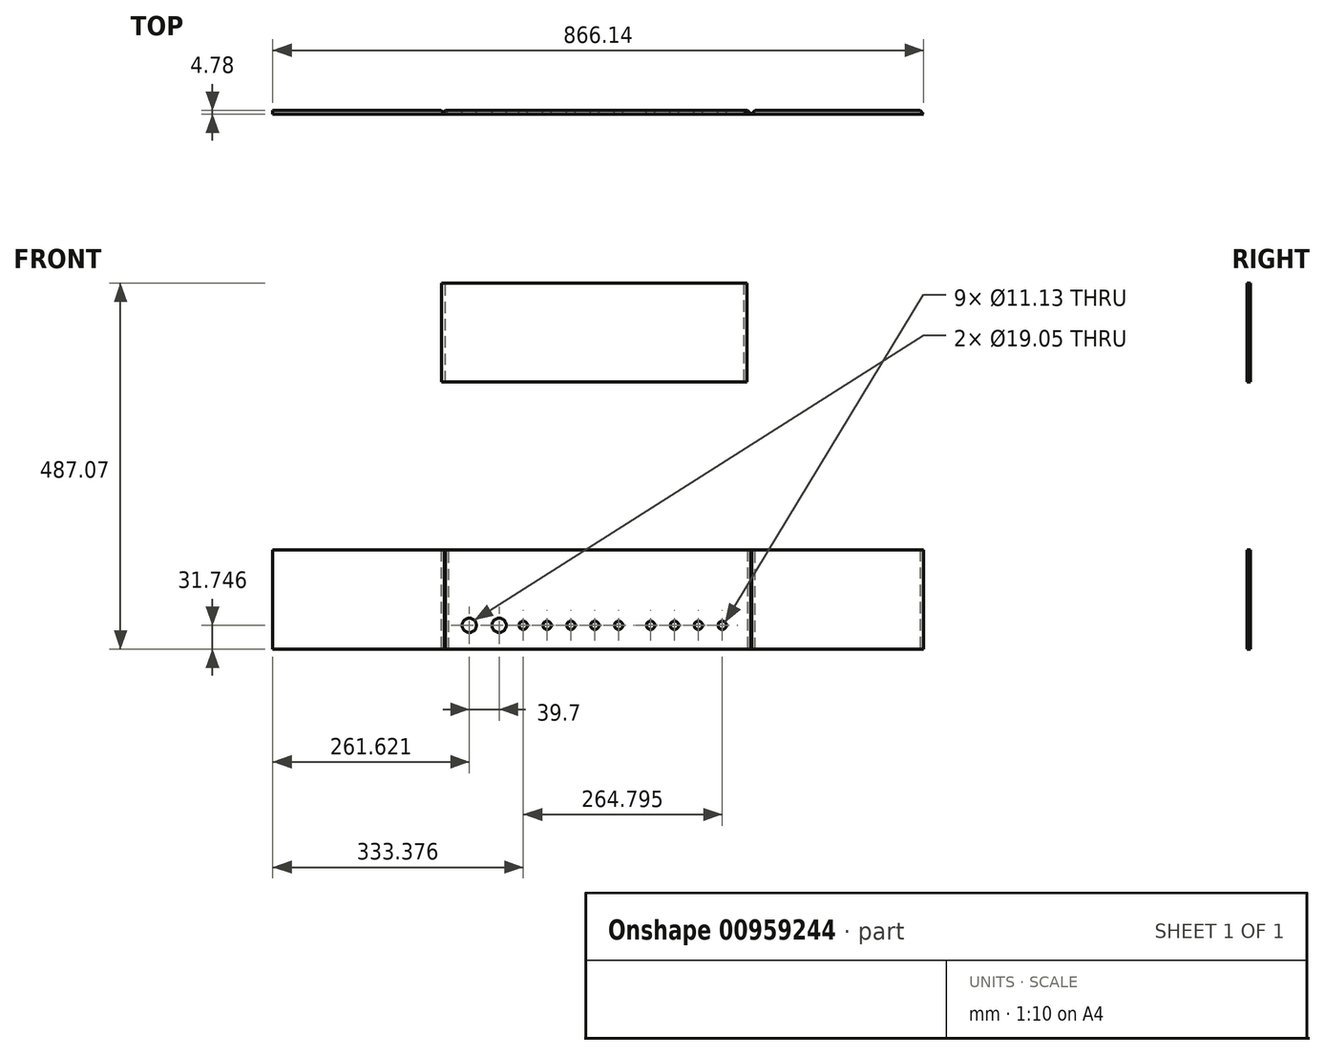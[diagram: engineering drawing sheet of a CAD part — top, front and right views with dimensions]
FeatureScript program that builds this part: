
annotation { "Feature Type Name" : "Feature", "Feature Type Description" : "" }
export const myFeature = defineFeature(function(context is Context, id is Id, definition is map)
    precondition{}
    {
        {
            var Q0;
            Q0=qCreatedBy(makeId("Front.planeOp"),FACE);
            var sketch = newSketch(context, id + "F0", { "sketchPlane" : qUnion([Q0])});
            skCircle(sketch, "E0", {"center": v(478.61, -8.53) * mm, "radius": 9.53 * mm});
            skCircle(sketch, "E1", {"center": v(518.31, -8.53) * mm, "radius": 9.53 * mm});
            skCircle(sketch, "E2", {"center": v(582.12, -8.53) * mm, "radius": 5.56 * mm});
            skCircle(sketch, "E3", {"center": v(613.87, -8.53) * mm, "radius": 5.56 * mm});
            skCircle(sketch, "E4", {"center": v(645.62, -8.53) * mm, "radius": 5.56 * mm});
            skPoint(sketch, "E5", {"position": v(677.37, -8.53) * mm});
            skCircle(sketch, "E6", {"center": v(677.37, -8.53) * mm, "radius": 5.56 * mm});
            skCircle(sketch, "E7", {"center": v(719.91, -8.53) * mm, "radius": 5.56 * mm});
            skCircle(sketch, "E8", {"center": v(751.66, -8.53) * mm, "radius": 5.56 * mm});
            skCircle(sketch, "E9", {"center": v(783.41, -8.53) * mm, "radius": 5.56 * mm});
            skCircle(sketch, "E10", {"center": v(815.16, -8.53) * mm, "radius": 5.56 * mm});
            skCircle(sketch, "E11", {"center": v(550.37, -8.53) * mm, "radius": 5.56 * mm});
            skLineSegment(sketch, "E12.right", {"start": v(446.86, 91.5) * mm, "end": v(446.86, -40.28) * mm});
            skLineSegment(sketch, "E13.bottom", {"start": v(446.86, 91.5) * mm, "end": v(853.26, 91.5) * mm});
            skLineSegment(sketch, "E13.top", {"start": v(446.86, -40.28) * mm, "end": v(853.26, -40.28) * mm});
            skLineSegment(sketch, "E14.bottom", {"start": v(854.53, 91.5) * mm, "end": v(1083.13, 91.5) * mm});
            skLineSegment(sketch, "E14.top", {"start": v(854.53, -40.28) * mm, "end": v(1083.13, -40.28) * mm});
            skLineSegment(sketch, "E14.left", {"start": v(854.53, 91.5) * mm, "end": v(854.53, -40.28) * mm});
            skLineSegment(sketch, "E14.right", {"start": v(1083.13, 91.5) * mm, "end": v(1083.13, -40.28) * mm});
            skLineSegment(sketch, "E15.bottom", {"start": v(217, 91.5) * mm, "end": v(445.6, 91.5) * mm});
            skLineSegment(sketch, "E15.top", {"start": v(217, -40.28) * mm, "end": v(445.6, -40.28) * mm});
            skLineSegment(sketch, "E15.left", {"start": v(848.18, 446.79) * mm, "end": v(848.18, 315.01) * mm});
            skLineSegment(sketch, "E16.bottom", {"start": v(441.78, 446.79) * mm, "end": v(848.18, 446.79) * mm});
            skLineSegment(sketch, "E16.left", {"start": v(441.78, 446.79) * mm, "end": v(441.78, 315.01) * mm});
            skLineSegment(sketch, "E17", {"start": v(217, 91.5) * mm, "end": v(217, -40.28) * mm});
            skLineSegment(sketch, "E18", {"start": v(445.6, 91.5) * mm, "end": v(445.6, -40.28) * mm});
            skLineSegment(sketch, "E19", {"start": v(853.26, 91.5) * mm, "end": v(853.26, -40.28) * mm});
            skLineSegment(sketch, "E20.right", {"start": v(217, -40.28) * mm, "end": v(217, 91.5) * mm});
            skLineSegment(sketch, "E21.bottom", {"start": v(445.6, 91.5) * mm, "end": v(446.86, 91.5) * mm});
            skLineSegment(sketch, "E21.top", {"start": v(445.6, -40.28) * mm, "end": v(446.86, -40.28) * mm});
            skLineSegment(sketch, "E22.bottom", {"start": v(853.26, 91.5) * mm, "end": v(854.53, 91.5) * mm});
            skLineSegment(sketch, "E22.top", {"start": v(853.26, -40.28) * mm, "end": v(854.53, -40.28) * mm});
            skLineSegment(sketch, "E23", {"start": v(441.78, 315.01) * mm, "end": v(848.18, 315.01) * mm});
            skSolve(sketch);
        }
        {
            var Q0;
            Q0=makeQuery(id+"F0.imprint","IMPRINT",FACE,{"disambiguationData":[TD([[makeQuery(id+"F0.imprint","IMPRINT",EDGE,{"derivedFrom":sQuery(id+"F0.wireOp",EDGE,"E16.bottom")}),-1.0]])]});
            var Q1;
            Q1=makeQuery(id+"F0.imprint","IMPRINT",FACE,{"disambiguationData":[TD([[makeQuery(id+"F0.imprint","IMPRINT",EDGE,{"derivedFrom":sQuery(id+"F0.wireOp",EDGE,"E15.bottom")}),-1.0]])]});
            var Q2;
            Q2=makeQuery(id+"F0.imprint","IMPRINT",FACE,{"disambiguationData":[TD([[makeQuery(id+"F0.imprint","IMPRINT",EDGE,{"derivedFrom":sQuery(id+"F0.wireOp",EDGE,"E0")}),-1.0]])]});
            var Q3;
            Q3=makeQuery(id+"F0.imprint","IMPRINT",FACE,{"disambiguationData":[TD([[makeQuery(id+"F0.imprint","IMPRINT",EDGE,{"derivedFrom":sQuery(id+"F0.wireOp",EDGE,"E14.bottom")}),-1.0]])]});
            extrude(context, id + "F1", {"entities" : qUnion([Q0, Q1, Q2, Q3]), "depth" : 4.78 * mm, "offsetDistance" : 25.4 * mm});
        }
        {
            var Q0;
            Q0=makeQuery(id+"F0.imprint","IMPRINT",FACE,{"disambiguationData":[TD([[makeQuery(id+"F0.imprint","IMPRINT",EDGE,{"derivedFrom":sQuery(id+"F0.wireOp",EDGE,"E20.bottom")}),1.0]])]});
            var Q1;
            Q1=makeQuery(id+"F0.imprint","IMPRINT",FACE,{"disambiguationData":[TD([[makeQuery(id+"F0.imprint","IMPRINT",EDGE,{"derivedFrom":sQuery(id+"F0.wireOp",EDGE,"E21.bottom")}),-1.0]])]});
            var Q2;
            Q2=makeQuery(id+"F0.imprint","IMPRINT",FACE,{"disambiguationData":[TD([[makeQuery(id+"F0.imprint","IMPRINT",EDGE,{"derivedFrom":sQuery(id+"F0.wireOp",EDGE,"E22.bottom")}),-1.0]])]});
            extrude(context, id + "F2", {"entities" : qUnion([Q0, Q1, Q2]), "depth" : 0 * mm, "offsetDistance" : 25.4 * mm, "hasSecondDirection" : true, "secondDirectionOppositeDirection" : true, "secondDirectionDepth" : 0.25 * mm});
        }
        {
            var Q0;
            Q0=makeQuery(id+"F1.opExtrude","CAP_EDGE",EDGE,{"disambiguationData":[OSD([sQuery(id+"F0.wireOp",EDGE,"E20.right")])],"isStart":true});
            var Q1;
            Q1=makeQuery(id+"F1.opExtrude","CAP_EDGE",EDGE,{"disambiguationData":[OSD([sQuery(id+"F0.wireOp",EDGE,"E14.right")])],"isStart":true});
            var Q2;
            Q2=makeQuery(id+"F1.opExtrude","CAP_EDGE",EDGE,{"disambiguationData":[OSD([sQuery(id+"F0.wireOp",EDGE,"E15.left")])],"isStart":true});
            var Q3;
            Q3=makeQuery(id+"F1.opExtrude","CAP_EDGE",EDGE,{"disambiguationData":[OSD([sQuery(id+"F0.wireOp",EDGE,"E16.left")])],"isStart":true});
            chamfer(context, id + "F3", {"entities" : qUnion([Q0, Q1, Q2, Q3]), "width" : 4.78 * mm, "tangentPropagation" : true});
        }
        {
            var Q0;
            Q0=makeQuery(id+"F2.opExtrude","SWEPT_BODY",BODY,{"disambiguationData":[OSD([sQuery(id+"F0.wireOp",EDGE,"E21.bottom"),sQuery(id+"F0.wireOp",EDGE,"E21.top"),sQuery(id+"F0.wireOp",EDGE,"E18"),sQuery(id+"F0.wireOp",EDGE,"E12.right")])]});
            var Q1;
            Q1=makeQuery(id+"F2.opExtrude","SWEPT_BODY",BODY,{"disambiguationData":[OSD([sQuery(id+"F0.wireOp",EDGE,"E22.bottom"),sQuery(id+"F0.wireOp",EDGE,"E22.top"),sQuery(id+"F0.wireOp",EDGE,"E19"),sQuery(id+"F0.wireOp",EDGE,"E14.left")])]});
            transform(context, id + "F4", {"entities" : qUnion([Q0, Q1]), "transformType" : TransformType.TRANSLATION_3D, "dx" : 0 * mm, "dy" : -4.78 * mm, "dz" : 0 * mm, "makeCopy" : false});
        }
        {
            var Q0;
            Q0=makeQuery(id+"F1.opExtrude","CAP_EDGE",EDGE,{"disambiguationData":[OSD([sQuery(id+"F0.wireOp",EDGE,"E18")])],"isStart":true});
            var Q1;
            Q1=makeQuery(id+"F1.opExtrude","CAP_EDGE",EDGE,{"disambiguationData":[OSD([sQuery(id+"F0.wireOp",EDGE,"E12.right")])],"isStart":true});
            var Q2;
            Q2=makeQuery(id+"F1.opExtrude","CAP_EDGE",EDGE,{"disambiguationData":[OSD([sQuery(id+"F0.wireOp",EDGE,"E19")])],"isStart":true});
            var Q3;
            Q3=makeQuery(id+"F1.opExtrude","CAP_EDGE",EDGE,{"disambiguationData":[OSD([sQuery(id+"F0.wireOp",EDGE,"E14.left")])],"isStart":true});
            chamfer(context, id + "F5", {"entities" : qUnion([Q0, Q1, Q2, Q3]), "width" : 4.52 * mm, "tangentPropagation" : true});
        }
    });
